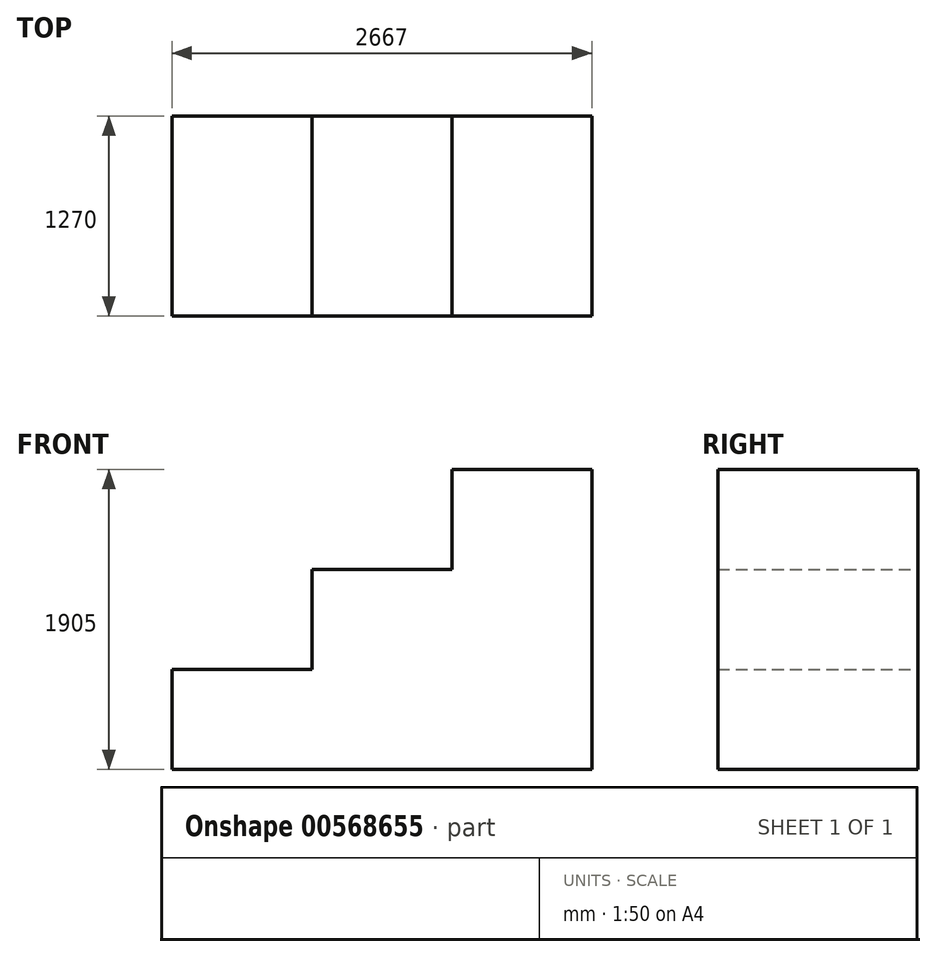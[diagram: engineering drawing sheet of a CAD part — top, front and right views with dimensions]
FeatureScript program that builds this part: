
annotation { "Feature Type Name" : "Feature", "Feature Type Description" : "" }
export const myFeature = defineFeature(function(context is Context, id is Id, definition is map)
    precondition{}
    {
        {
            var Q0;
            Q0=qCreatedBy(makeId("Front.planeOp"),FACE);
            var sketch = newSketch(context, id + "F0", { "sketchPlane" : qUnion([Q0])});
            skLineSegment(sketch, "E0", {"start": v(0, 0) * mm, "end": v(2667, 0) * mm});
            skLineSegment(sketch, "E1", {"start": v(2667, 0) * mm, "end": v(2667, 1905) * mm});
            skLineSegment(sketch, "E2", {"start": v(2667, 1905) * mm, "end": v(1778, 1905) * mm});
            skLineSegment(sketch, "E3", {"start": v(1778, 1905) * mm, "end": v(1778, 1270) * mm});
            skLineSegment(sketch, "E4", {"start": v(1778, 1270) * mm, "end": v(889, 1270) * mm});
            skLineSegment(sketch, "E5", {"start": v(889, 1270) * mm, "end": v(889, 635) * mm});
            skLineSegment(sketch, "E6", {"start": v(889, 635) * mm, "end": v(0, 635) * mm});
            skLineSegment(sketch, "E7", {"start": v(0, 635) * mm, "end": v(0, 0) * mm});
            skSolve(sketch);
        }
        {
            var Q0;
            Q0 = qSketchRegion(id + "F0", true);
            extrude(context, id + "F1", {"entities" : qUnion([Q0]), "depth" : 1270 * mm, "offsetDistance" : 25.4 * mm});
        }
    });
